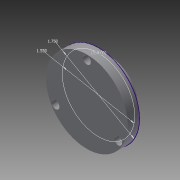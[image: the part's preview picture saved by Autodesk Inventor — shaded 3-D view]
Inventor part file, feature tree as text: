
AUTODESK INVENTOR PART (.ipt)
format: ipt  version: 2015 (Build 190159000, 159)  size: 94,720 bytes
history: native  units: in
note: dims shown in document units (in); Inventor stores cm internally (conversion verified against a paired STEP export)
features: sketch x2, extrude x2, hole x1
ambient origin geometry x8: Origin, YZ Plane, XZ Plane, XY Plane, X Axis, Y Axis, Z Axis, Center Point
bodies: Solid1 (feature_tree)
feature tree (5):
  sketch  "Sketch1"  dims[d0=1.75in d1=1.55in]
  extrude  "Extrusion1"  Depth=1.55in
  extrude  "Extrusion2"  Depth=0.25in TaperAngle=0.0deg
  hole  "Hole1"  [1 undecoded]
  sketch  "Sketch2"  dims[d2=1.1811in d4=360.0deg d6=0.25in d7=0.0in d8=1.165in d9=0.25in d10=0.0in d11=0.172in d12=0.75in d13=0.375in d14=0.25in d15=0.5635in d16=1.0in d17=0.8108in]
note: 1 required parameter value undecoded (feature->parameter linkage not recoverable at this tier; creation-order binding heuristic only, values carry confidence <= 0.55)
